# Revit family: Loading-Dock-Equipment_Shelter_McGuire_TC900
name_source: partatom
category: Generic Models
units: mm (PartAtom-declared; Revit-internal decimal feet)

## family parameters
Always vertical = No
Can host rebar = No
Classification Number = 23.50.70.00
Cut with Voids When Loaded = No
Maintain Annotation Orientation = No
Part Type = Normal
Room Calculation Point = No
Round Connector Dimension = Use Diameter
Shared = No
Work Plane-Based = Yes

## types (2) — shared parameters
Assembly Code = E1030300
Default Elevation = 0' - 0"
Description = McGuire Loading Dock Product as Specified
Green Building-LEED = http://www.arcat.com
Guide Color = Polyethylene Sheeting - Yellow
Keynote = 11160
Manufacturer = McGuire
Manufacturer Fax = 262-255-4199
Manufacturer Website = http://www.wbmcguire.com
Material = Polyethylene Sheeting - Black
Model = As Specified
Panel Material = Metal - Steel
Product Data = http://www.arcat.com
Revision = R1_2017-01
Sales Information = http://www.wbmcguire.com
URL = http://www.wbmcguire.com
zero-valued in all types: Expected Lifespan (Years), Maintenance Schedule (Months), Warranty Duration (Years)

## per-type parameters (varying)
| type | Accent Material | Frame Thickness |
| Flexible Soft Sides Wood Frame | Metal - Aluminum Trim | 0' - 4" |
| Flexible Soft Sides Steel Frame | Translucent Fiberglass | 0' - 6" |

## geometry (parser evidence)
native form markers: Blend x14, Sweep x1
no freeform markers — native parametric forms only
